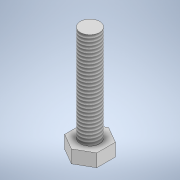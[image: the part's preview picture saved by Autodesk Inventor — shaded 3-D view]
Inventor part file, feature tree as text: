
AUTODESK INVENTOR PART (.ipt)
format: ipt  version: 2020.2 (Build 242310000, 310)  size: 113,664 bytes
history: native  units: mm
features: extrude x2, sketch x2, thread x1
ambient origin geometry x8: Origin, YZ Plane, XZ Plane, XY Plane, X Axis, Y Axis, Z Axis, Center Point
bodies: Solido1 (feature_tree)
feature tree (5):
  extrude  "Estrusione1"  Depth=10.0mm
  extrude  "Estrusione2"  Depth=4.0mm TaperAngle=0.0deg
  thread  "Filettatura1"
  sketch  "Schizzo1"
  sketch  "Schizzo2"
